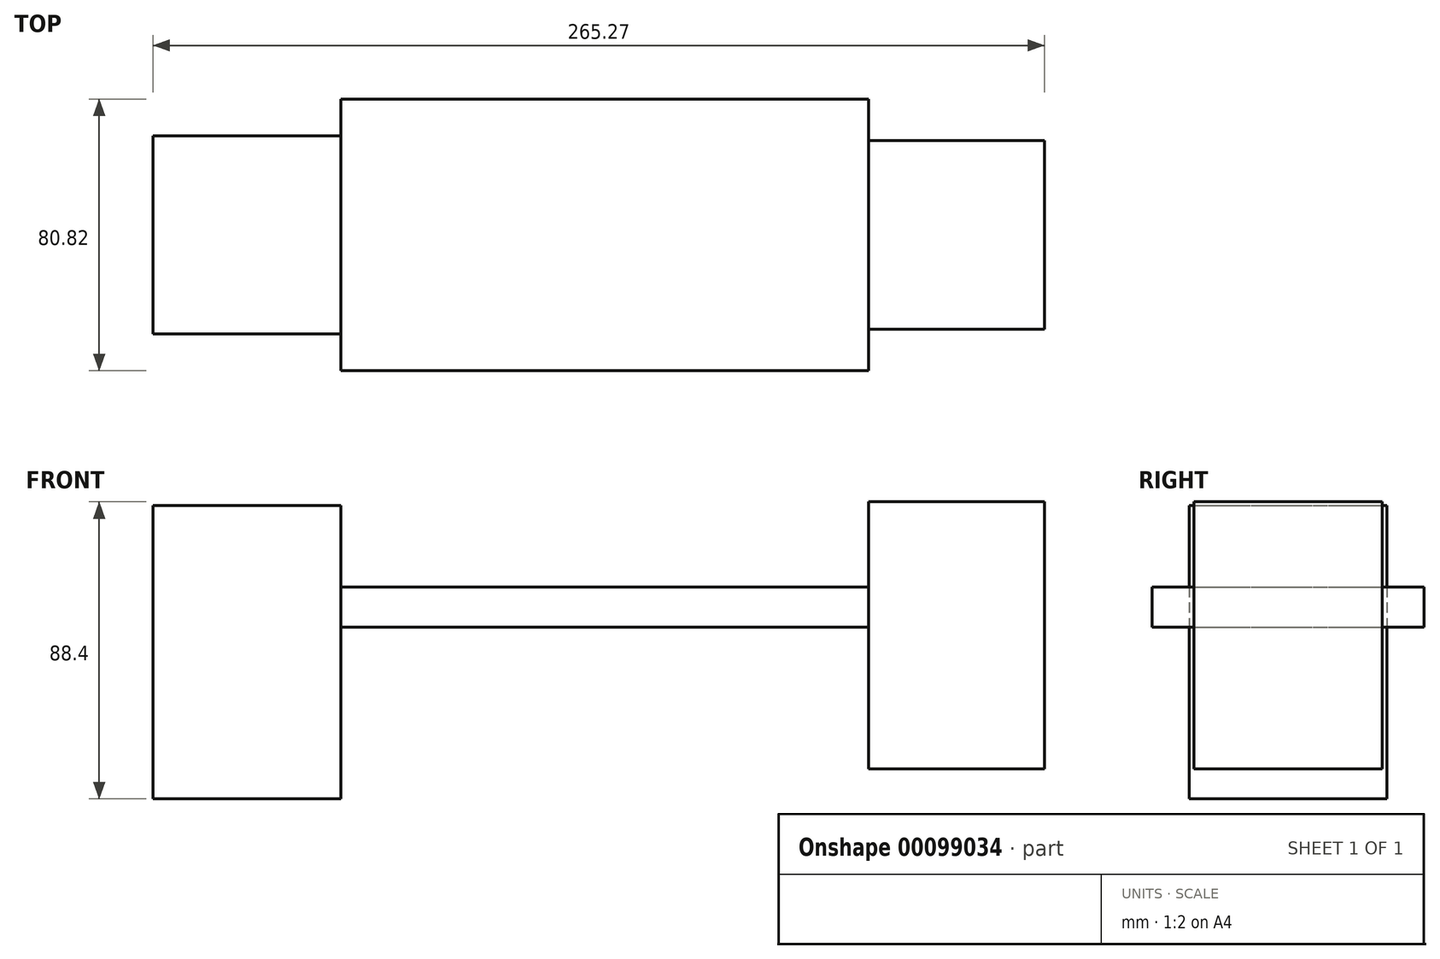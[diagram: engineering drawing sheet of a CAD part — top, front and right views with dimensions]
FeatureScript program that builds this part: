
annotation { "Feature Type Name" : "Feature", "Feature Type Description" : "" }
export const myFeature = defineFeature(function(context is Context, id is Id, definition is map)
    precondition{}
    {
        {
            var Q0;
            Q0=qCreatedBy(makeId("Top.planeOp"),FACE);
            var sketch = newSketch(context, id + "F0", { "sketchPlane" : qUnion([Q0])});
            skLineSegment(sketch, "E0.bottom", {"start": v(-78.47, -40.41) * mm, "end": v(78.47, -40.41) * mm});
            skLineSegment(sketch, "E0.top", {"start": v(-78.47, 40.41) * mm, "end": v(78.47, 40.41) * mm});
            skLineSegment(sketch, "E0.left", {"start": v(-78.47, -40.41) * mm, "end": v(-78.47, 40.41) * mm});
            skLineSegment(sketch, "E0.right", {"start": v(78.47, -40.41) * mm, "end": v(78.47, 40.41) * mm});
            skPoint(sketch, "E0.middle", {"position": v(0, 0) * mm});
            skSolve(sketch);
        }
        {
            var Q0;
            Q0=makeQuery(id+"F0.imprint","IMPRINT",FACE,{"disambiguationData":[TD([[makeQuery(id+"F0.imprint","IMPRINT",EDGE,{"derivedFrom":sQuery(id+"F0.wireOp",EDGE,"E0.bottom")}),1.0]])]});
            extrude(context, id + "F1", {"entities" : qUnion([Q0]), "depth" : 11.87 * mm});
        }
        {
            var Q0;
            Q0=makeQuery(id+"F1.opExtrude","CAP_FACE",FACE,{"disambiguationData":[OSD([sQuery(id+"F0.wireOp",EDGE,"E0.bottom"),sQuery(id+"F0.wireOp",EDGE,"E0.top"),sQuery(id+"F0.wireOp",EDGE,"E0.left"),sQuery(id+"F0.wireOp",EDGE,"E0.right")])],"isStart":false});
            var sketch = newSketch(context, id + "F2", { "sketchPlane" : qUnion([Q0])});
            skLineSegment(sketch, "E1.bottom", {"start": v(-64.46, -29.44) * mm, "end": v(-134.4, -29.44) * mm});
            skLineSegment(sketch, "E1.top", {"start": v(-64.46, 29.44) * mm, "end": v(-134.4, 29.44) * mm});
            skLineSegment(sketch, "E1.left", {"start": v(-64.46, -29.44) * mm, "end": v(-64.46, 29.44) * mm});
            skLineSegment(sketch, "E1.right", {"start": v(-134.4, -29.44) * mm, "end": v(-134.4, 29.44) * mm});
            skPoint(sketch, "E1.middle", {"position": v(-99.43, 0) * mm});
            skSolve(sketch);
        }
        {
            var Q0;
            {var subQ1=sQuery(id+"F2.wireOp",EDGE,"E1.left");Q0=makeQuery(id+"F2.imprint","IMPRINT",FACE,{"disambiguationData":[TD([[makeQuery(id+"F2.imprint","IMPRINT",EDGE,{"derivedFrom":subQ1}),-1.0]])]});}
            var sketch = newSketch(context, id + "F3", { "sketchPlane" : qUnion([Q0])});
            skLineSegment(sketch, "E2.bottom", {"start": v(64.9, -28.02) * mm, "end": v(130.87, -28.02) * mm});
            skLineSegment(sketch, "E2.top", {"start": v(64.9, 28.02) * mm, "end": v(130.87, 28.02) * mm});
            skLineSegment(sketch, "E2.left", {"start": v(64.9, -28.02) * mm, "end": v(64.9, 28.02) * mm});
            skLineSegment(sketch, "E2.right", {"start": v(130.87, -28.02) * mm, "end": v(130.87, 28.02) * mm});
            skPoint(sketch, "E2.middle", {"position": v(97.89, 0) * mm});
            skSolve(sketch);
        }
        {
            var Q0;
            {var subQ0=sQuery(id+"F2.wireOp",EDGE,"E1.right");Q0=makeQuery(id+"F2.imprint","IMPRINT",FACE,{"disambiguationData":[TD([[makeQuery(id+"F2.imprint","IMPRINT",EDGE,{"derivedFrom":subQ0}),-1.0]])]});}
            extrude(context, id + "F4", {"entities" : qUnion([Q0]), "operationType" : NewBodyOperationType.ADD, "depth" : 24.28 * mm, "hasSecondDirection" : true, "secondDirectionOppositeDirection" : true, "secondDirectionDepth" : 63 * mm});
        }
        {
            var Q0;
            {var subQ0=sQuery(id+"F3.wireOp",EDGE,"E2.right");Q0=makeQuery(id+"F3.imprint","IMPRINT",FACE,{"disambiguationData":[TD([[makeQuery(id+"F3.imprint","IMPRINT",EDGE,{"derivedFrom":subQ0}),1.0]])]});}
            extrude(context, id + "F5", {"entities" : qUnion([Q0]), "operationType" : NewBodyOperationType.ADD, "depth" : 25.4 * mm, "hasSecondDirection" : true, "secondDirectionOppositeDirection" : true, "secondDirectionDepth" : 54.02 * mm});
        }
    });
